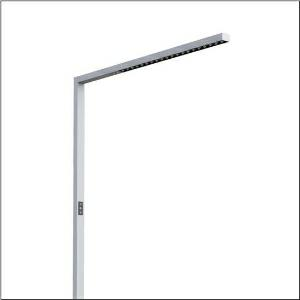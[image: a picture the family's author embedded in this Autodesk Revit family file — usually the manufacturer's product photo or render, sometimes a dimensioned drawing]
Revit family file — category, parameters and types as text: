
# Revit family: silica_r__31_floor_51my52fa4cs_7d3f
name_source: partatom
category: Lighting Fixtures
units: mm (PartAtom-declared; Revit-internal decimal feet)

## family parameters
Cut with Voids When Loaded = No
Host = Face
Light Source = No
Part Type = Normal
Room Calculation Point = No
Round Connector Dimension = Use Diameter
Shared = No

## types (1)
- Silica® 31 Floor (1 x LED, 10600 lm, 75 W, 4000K)
    Apparent Load = 75 VA
    CIE Flux Codes = 86 100 100 24 100
    Color Rendering = 80
    Color Temperature = 4000K
    Default Elevation = 1800 mm
    Description = Silica® 31 Floor, floorstanding luminaire, secondary optical cover: cover panel, of PMMA, light emission: direct/indirect distribution, primary light characteristic: symmetric, installation type: not mounted, LED, rated luminous flux: 10.600lm, luminous efficacy: 141lm/W, light colour: 840, colour temperature: 4000K, control gear: Touchdim, daylight-dependent control, with cable with plug, mains connection: 230V, AC, 50Hz, connection cable pre-assembled, rated input power: 75W, luminaire head, of aluminium, metallic grey (RAL 9006), length: 1.203mm, width: 52mm, supporting column, angular, of aluminium, metallic grey (RAL 9006), baseplate, of steel, metallic grey (RAL 9006), protection rating (complete): IP20, insulation class (complete): insulation class I (protective earthing), certification: CE, permissible operating ambient temperature: -20..+40°C, standard: EN 50419, packaging unit: 1 piece
    Height = 36 mm
    Lamp = 1 x LED
    Lamp Light Flux = 10600 lm
    Lamp Power = 75 W
    Lamp count = 1
    Length = 1203 mm
    Luminous efficacy = 141 lm/W
    Manufacturer = Siteco
    ModVariant = No
    Model = 51MY52FA4CS
    Mounting Place = Floor
    Mounting Type = Freestanding
    Number of Poles = 1
    OnlyDefault = Yes
    Power Factor = 1
    Product Name = Silica® 31 Floor
    Product group = floorstanding luminaire
    ProductGroupID = 1302
    Protection Class = Protection class I
    Protection Degree = IP 20
    RLX_Detail_Level = 1
    RLX_Emergency_Light_Flux = 0 lm
    RLX_Emergency_Type = 0
    RLX_Emergency_Type_DB = No
    RlxData = <blob elided: 19601 chars, md5=3c6f073b>
    Socket = socket
    Standby Power = 0 W
    System Light Flux = 10600 lm
    System Power = 75 W
    Type Comments = Product without accessories
    Type Image = l_1275303.jpg
    URL = http://relux.com
    VarID = ---
    Voltage = 0 V
    Weight = 0.00 kg
    Width = 52 mm  [stored 0.170604 ft]

note: [stored X ft] marks values corroborated as IEEE doubles in the binary element streams (Revit-internal decimal feet)

## geometry (parser evidence)
native form markers: Blend x4, Sweep x14
no freeform markers — native parametric forms only
